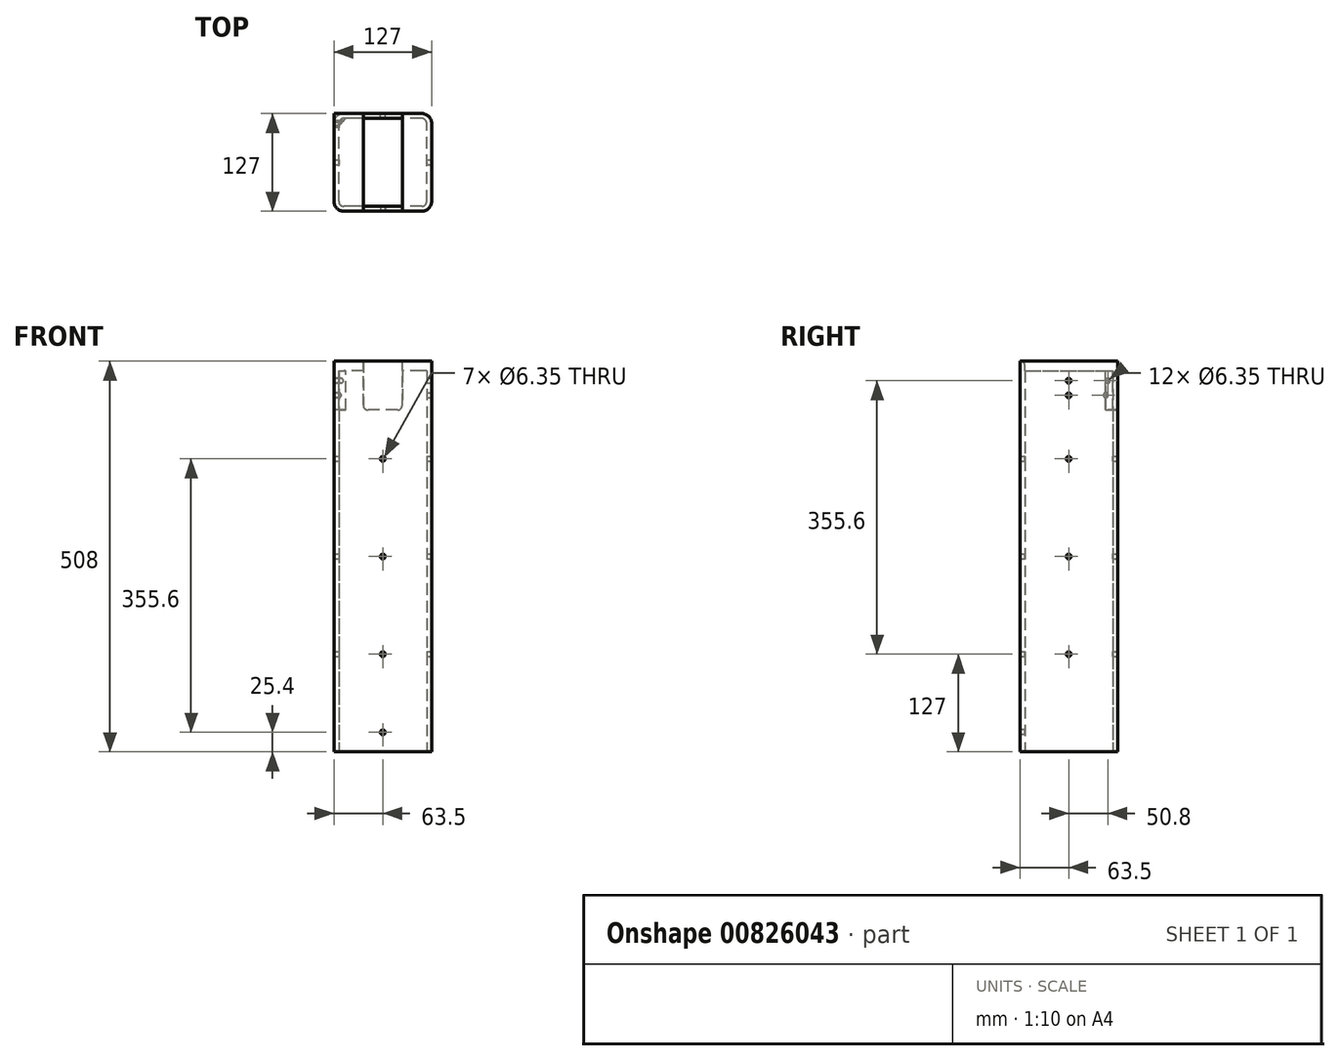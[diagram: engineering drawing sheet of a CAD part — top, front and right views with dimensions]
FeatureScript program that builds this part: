
annotation { "Feature Type Name" : "Feature", "Feature Type Description" : "" }
export const myFeature = defineFeature(function(context is Context, id is Id, definition is map)
    precondition{}
    {
        {
            var Q0;
            Q0=qCreatedBy(makeId("Top.planeOp"),FACE);
            var sketch = newSketch(context, id + "F0", { "sketchPlane" : qUnion([Q0])});
            skLineSegment(sketch, "E0.bottom", {"start": v(50.8, -63.5) * mm, "end": v(-50.8, -63.5) * mm});
            skLineSegment(sketch, "E0.top", {"start": v(50.8, 63.5) * mm, "end": v(-50.8, 63.5) * mm});
            skLineSegment(sketch, "E0.left", {"start": v(63.5, -50.8) * mm, "end": v(63.5, 50.8) * mm});
            skLineSegment(sketch, "E0.right", {"start": v(-63.5, -50.8) * mm, "end": v(-63.5, 50.8) * mm});
            skPoint(sketch, "E0.middle", {"position": v(0, 0) * mm});
            skPoint(sketch, "E1.visualSharp", {"position": v(-63.5, 63.5) * mm});
            skArc(sketch, "E1.filletArc", {"start": v(-50.8, 63.5) * mm, "mid": v(-59.78, 59.78) * mm, "end": v(-63.5, 50.8) * mm});
            skPoint(sketch, "E2.visualSharp", {"position": v(-63.5, -63.5) * mm});
            skArc(sketch, "E2.filletArc", {"start": v(-63.5, -50.8) * mm, "mid": v(-59.78, -59.78) * mm, "end": v(-50.8, -63.5) * mm});
            skPoint(sketch, "E3.visualSharp", {"position": v(63.5, 63.5) * mm});
            skArc(sketch, "E3.filletArc", {"start": v(63.5, 50.8) * mm, "mid": v(59.78, 59.78) * mm, "end": v(50.8, 63.5) * mm});
            skPoint(sketch, "E4.visualSharp", {"position": v(63.5, -63.5) * mm});
            skArc(sketch, "E4.filletArc", {"start": v(50.8, -63.5) * mm, "mid": v(59.78, -59.78) * mm, "end": v(63.5, -50.8) * mm});
            skArc(sketch, "E5.0", {"start": v(57.15, 50.8) * mm, "mid": v(55.3, 55.3) * mm, "end": v(50.8, 57.15) * mm});
            skLineSegment(sketch, "E5.1", {"start": v(57.15, -50.8) * mm, "end": v(57.15, 50.8) * mm});
            skLineSegment(sketch, "E5.2", {"start": v(50.8, 57.15) * mm, "end": v(-50.8, 57.15) * mm});
            skArc(sketch, "E5.3", {"start": v(50.8, -57.15) * mm, "mid": v(55.3, -55.3) * mm, "end": v(57.15, -50.8) * mm});
            skArc(sketch, "E5.4", {"start": v(-50.8, 57.15) * mm, "mid": v(-55.3, 55.3) * mm, "end": v(-57.15, 50.8) * mm});
            skLineSegment(sketch, "E5.5", {"start": v(-57.15, -50.8) * mm, "end": v(-57.15, 50.8) * mm});
            skArc(sketch, "E5.6", {"start": v(-57.15, -50.8) * mm, "mid": v(-55.3, -55.3) * mm, "end": v(-50.8, -57.15) * mm});
            skLineSegment(sketch, "E5.7", {"start": v(50.8, -57.15) * mm, "end": v(-50.8, -57.15) * mm});
            skSolve(sketch);
        }
        {
            var Q0;
            Q0 = qSketchRegion(id + "F0", true);
            extrude(context, id + "F1", {"entities" : qUnion([Q0]), "depth" : 254 * mm, "offsetDistance" : 25.4 * mm, "hasSecondDirection" : true, "secondDirectionOppositeDirection" : true, "secondDirectionDepth" : 254 * mm});
        }
        {
            var Q0;
            Q0=qCreatedBy(makeId("Front.planeOp"),FACE);
            var sketch = newSketch(context, id + "F2", { "sketchPlane" : qUnion([Q0])});
            skLineSegment(sketch, "E6.0", {"start": v(-63.5, 254) * mm, "end": v(63.5, 254) * mm});
            skLineSegment(sketch, "E7.0", {"start": v(-63.5, -0.89) * mm, "end": v(63.5, -0.89) * mm});
            skLineSegment(sketch, "E8", {"start": v(63.5, 236.04) * mm, "end": v(63.5, -0.89) * mm});
            skLineSegment(sketch, "E9", {"start": v(-63.5, 254) * mm, "end": v(-63.5, -0.89) * mm});
            skLineSegment(sketch, "E10", {"start": v(63.5, 254) * mm, "end": v(70.9, 261.4) * mm});
            skLineSegment(sketch, "E11.0", {"start": v(63.5, 236.04) * mm, "end": v(79.88, 252.42) * mm});
            skLineSegment(sketch, "E12", {"start": v(81.46, 262.98) * mm, "end": v(67.93, 249.45) * mm, "construction": true});
            skLineSegment(sketch, "E13", {"start": v(72.48, 262.98) * mm, "end": v(81.46, 262.98) * mm, "construction": true});
            skArc(sketch, "E14", {"start": v(83.16, 254.16) * mm, "mid": v(87.81, 269.33) * mm, "end": v(72.64, 264.68) * mm});
            skPoint(sketch, "E15.visualSharp", {"position": v(72.48, 262.98) * mm});
            skArc(sketch, "E15.filletArc", {"start": v(70.9, 261.4) * mm, "mid": v(72.02, 262.91) * mm, "end": v(72.64, 264.68) * mm});
            skPoint(sketch, "E16.visualSharp", {"position": v(81.46, 254) * mm});
            skArc(sketch, "E16.filletArc", {"start": v(83.16, 254.16) * mm, "mid": v(81.4, 253.54) * mm, "end": v(79.88, 252.42) * mm});
            skLineSegment(sketch, "E17", {"start": v(57.15, 254) * mm, "end": v(57.15, 236.04) * mm});
            skLineSegment(sketch, "E18", {"start": v(57.15, 236.04) * mm, "end": v(63.5, 236.04) * mm});
            skArc(sketch, "E19.0", {"start": v(76.08, 248.62) * mm, "mid": v(92.3, 273.82) * mm, "end": v(67.1, 257.6) * mm});
            skSolve(sketch);
        }
        {
            var Q0;
            Q0=makeQuery(id+"F1.opExtrude","CAP_FACE",FACE,{"disambiguationData":[OSD([sQuery(id+"F0.wireOp",EDGE,"E0.bottom"),sQuery(id+"F0.wireOp",EDGE,"E0.top"),sQuery(id+"F0.wireOp",EDGE,"E0.left"),sQuery(id+"F0.wireOp",EDGE,"E0.right"),sQuery(id+"F0.wireOp",EDGE,"E1.filletArc"),sQuery(id+"F0.wireOp",EDGE,"E2.filletArc"),sQuery(id+"F0.wireOp",EDGE,"E3.filletArc"),sQuery(id+"F0.wireOp",EDGE,"E4.filletArc"),sQuery(id+"F0.wireOp",EDGE,"E5.0"),sQuery(id+"F0.wireOp",EDGE,"E5.1"),sQuery(id+"F0.wireOp",EDGE,"E5.2"),sQuery(id+"F0.wireOp",EDGE,"E5.3"),sQuery(id+"F0.wireOp",EDGE,"E5.4"),sQuery(id+"F0.wireOp",EDGE,"E5.5"),sQuery(id+"F0.wireOp",EDGE,"E5.6"),sQuery(id+"F0.wireOp",EDGE,"E5.7")])],"isStart":false});
            var sketch = newSketch(context, id + "F3", { "sketchPlane" : qUnion([Q0])});
            skLineSegment(sketch, "E20", {"start": v(-63.5, 6.35) * mm, "end": v(-63.5, 50.8) * mm});
            skLineSegment(sketch, "E21", {"start": v(-63.5, -6.35) * mm, "end": v(-63.5, 6.35) * mm});
            skLineSegment(sketch, "E22", {"start": v(-63.5, -50.8) * mm, "end": v(-63.5, -6.35) * mm});
            skArc(sketch, "E23", {"start": v(-63.5, -50.8) * mm, "mid": v(-59.78, -59.78) * mm, "end": v(-50.8, -63.5) * mm});
            skLineSegment(sketch, "E24", {"start": v(50.8, -63.5) * mm, "end": v(25.4, -63.5) * mm});
            skArc(sketch, "E25", {"start": v(50.8, -63.5) * mm, "mid": v(59.78, -59.78) * mm, "end": v(63.5, -50.8) * mm});
            skLineSegment(sketch, "E26", {"start": v(63.5, -50.8) * mm, "end": v(63.5, -6.35) * mm});
            skLineSegment(sketch, "E27", {"start": v(63.5, -6.35) * mm, "end": v(63.5, 6.35) * mm});
            skLineSegment(sketch, "E28", {"start": v(63.5, 6.35) * mm, "end": v(63.5, 50.8) * mm});
            skArc(sketch, "E29", {"start": v(63.5, 50.8) * mm, "mid": v(59.78, 59.78) * mm, "end": v(50.8, 63.5) * mm});
            skLineSegment(sketch, "E30", {"start": v(50.8, 63.5) * mm, "end": v(25.4, 63.5) * mm});
            skArc(sketch, "E31", {"start": v(-50.8, 63.5) * mm, "mid": v(-59.78, 59.78) * mm, "end": v(-63.5, 50.8) * mm});
            skLineSegment(sketch, "E32", {"start": v(-25.4, -63.5) * mm, "end": v(-25.4, 63.5) * mm});
            skLineSegment(sketch, "E33", {"start": v(25.4, -63.5) * mm, "end": v(25.4, 63.5) * mm});
            skLineSegment(sketch, "E34.trimOffspring", {"start": v(-25.4, -63.5) * mm, "end": v(-50.8, -63.5) * mm});
            skLineSegment(sketch, "E35.trimOffspring", {"start": v(-25.4, 63.5) * mm, "end": v(-50.8, 63.5) * mm});
            skSolve(sketch);
        }
        {
            var Q0;
            {var subQ1=makeQuery(id+"F1.opExtrude","CAP_EDGE",EDGE,{"disambiguationData":[OSD([sQuery(id+"F0.wireOp",EDGE,"E5.0")])],"isStart":false});Q0=makeQuery(id+"F3.imprint","IMPRINT",FACE,{"disambiguationData":[TD([[makeQuery(id+"F3.imprint","IMPRINT",EDGE,{"derivedFrom":subQ1}),1.0]])]});}
            var Q1;
            {var subQ1=makeQuery(id+"F1.opExtrude","CAP_EDGE",EDGE,{"disambiguationData":[OSD([sQuery(id+"F0.wireOp",EDGE,"E5.4")])],"isStart":false});Q1=makeQuery(id+"F3.imprint","IMPRINT",FACE,{"disambiguationData":[TD([[makeQuery(id+"F3.imprint","IMPRINT",EDGE,{"derivedFrom":subQ1}),1.0]])]});}
            extrude(context, id + "F4", {"entities" : qUnion([Q0, Q1]), "operationType" : NewBodyOperationType.ADD, "oppositeDirection" : true, "depth" : 12.7 * mm, "offsetDistance" : 25.4 * mm});
        }
        {
            var Q0;
            Q0=makeQuery(id+"F1.opExtrude","SWEPT_FACE",FACE,{"disambiguationData":[OSD([sQuery(id+"F0.wireOp",EDGE,"E0.left")])]});
            var sketch = newSketch(context, id + "F5", { "sketchPlane" : qUnion([Q0])});
            skPoint(sketch, "E36", {"position": v(0, 228.6) * mm});
            skPoint(sketch, "E37", {"position": v(0, 209.55) * mm});
            skSolve(sketch);
        }
        {
            var Q0;
            Q0=sQuery(id+"F5.wireOp",VERTEX,"E37");
            var Q1;
            Q1=sQuery(id+"F5.wireOp",VERTEX,"E36");
            var Q2;
            Q2=makeQuery(id+"F1.opExtrude","SWEPT_BODY",BODY,{"disambiguationData":[OSD([sQuery(id+"F0.wireOp",EDGE,"E0.bottom"),sQuery(id+"F0.wireOp",EDGE,"E0.top"),sQuery(id+"F0.wireOp",EDGE,"E0.left"),sQuery(id+"F0.wireOp",EDGE,"E0.right"),sQuery(id+"F0.wireOp",EDGE,"E1.filletArc"),sQuery(id+"F0.wireOp",EDGE,"E2.filletArc"),sQuery(id+"F0.wireOp",EDGE,"E3.filletArc"),sQuery(id+"F0.wireOp",EDGE,"E4.filletArc"),sQuery(id+"F0.wireOp",EDGE,"E5.0"),sQuery(id+"F0.wireOp",EDGE,"E5.1"),sQuery(id+"F0.wireOp",EDGE,"E5.2"),sQuery(id+"F0.wireOp",EDGE,"E5.3"),sQuery(id+"F0.wireOp",EDGE,"E5.4"),sQuery(id+"F0.wireOp",EDGE,"E5.5"),sQuery(id+"F0.wireOp",EDGE,"E5.6"),sQuery(id+"F0.wireOp",EDGE,"E5.7")])]});
            hole(context, id + "F6", {"style" : HoleStyle.SIMPLE, "endStyle" : HoleEndStyle.THROUGH, "holeDiameter" : 6.35 * mm, "majorDiameter" : 6.35 * mm, "isTappedThrough" : true, "tappedDepth" : 12.7 * mm, "tapClearance" : 3, "locations" : qUnion([Q0, Q1]), "scope" : qUnion([Q2])});
        }
        {
            var Q0;
            Q0=makeQuery(id+"F1.opExtrude","SWEPT_FACE",FACE,{"disambiguationData":[OSD([sQuery(id+"F0.wireOp",EDGE,"E0.bottom")])]});
            var sketch = newSketch(context, id + "F7", { "sketchPlane" : qUnion([Q0])});
            skPoint(sketch, "E38", {"position": v(0, -228.6) * mm});
            skSolve(sketch);
        }
        {
            var Q0;
            Q0=sQuery(id+"F7.wireOp",VERTEX,"E38");
            var Q1;
            Q1=makeQuery(id+"F1.opExtrude","SWEPT_BODY",BODY,{"disambiguationData":[OSD([sQuery(id+"F0.wireOp",EDGE,"E0.bottom"),sQuery(id+"F0.wireOp",EDGE,"E0.top"),sQuery(id+"F0.wireOp",EDGE,"E0.left"),sQuery(id+"F0.wireOp",EDGE,"E0.right"),sQuery(id+"F0.wireOp",EDGE,"E1.filletArc"),sQuery(id+"F0.wireOp",EDGE,"E2.filletArc"),sQuery(id+"F0.wireOp",EDGE,"E3.filletArc"),sQuery(id+"F0.wireOp",EDGE,"E4.filletArc"),sQuery(id+"F0.wireOp",EDGE,"E5.0"),sQuery(id+"F0.wireOp",EDGE,"E5.1"),sQuery(id+"F0.wireOp",EDGE,"E5.2"),sQuery(id+"F0.wireOp",EDGE,"E5.3"),sQuery(id+"F0.wireOp",EDGE,"E5.4"),sQuery(id+"F0.wireOp",EDGE,"E5.5"),sQuery(id+"F0.wireOp",EDGE,"E5.6"),sQuery(id+"F0.wireOp",EDGE,"E5.7")])]});
            hole(context, id + "F8", {"style" : HoleStyle.SIMPLE, "endStyle" : HoleEndStyle.BLIND, "holeDiameter" : 6.35 * mm, "majorDiameter" : 6.35 * mm, "holeDepth" : 12.7 * mm, "isTappedThrough" : true, "tappedDepth" : 12.7 * mm, "tapClearance" : 3, "locations" : qUnion([Q0]), "scope" : qUnion([Q1])});
        }
        {
            var Q0;
            Q0=makeQuery(id+"F1.opExtrude","SWEPT_FACE",FACE,{"disambiguationData":[OSD([sQuery(id+"F0.wireOp",EDGE,"E0.left")])]});
            var sketch = newSketch(context, id + "F9", { "sketchPlane" : qUnion([Q0])});
            skPoint(sketch, "E39", {"position": v(0, 0) * mm});
            skPoint(sketch, "E40", {"position": v(0, 127) * mm});
            skPoint(sketch, "E41", {"position": v(0, -127) * mm});
            skSolve(sketch);
        }
        {
            var Q0;
            Q0=sQuery(id+"F9.wireOp",VERTEX,"E39");
            var Q1;
            Q1=sQuery(id+"F9.wireOp",VERTEX,"E41");
            var Q2;
            Q2=sQuery(id+"F9.wireOp",VERTEX,"E40");
            var Q3;
            Q3=makeQuery(id+"F1.opExtrude","SWEPT_BODY",BODY,{"disambiguationData":[OSD([sQuery(id+"F0.wireOp",EDGE,"E0.bottom"),sQuery(id+"F0.wireOp",EDGE,"E0.top"),sQuery(id+"F0.wireOp",EDGE,"E0.left"),sQuery(id+"F0.wireOp",EDGE,"E0.right"),sQuery(id+"F0.wireOp",EDGE,"E1.filletArc"),sQuery(id+"F0.wireOp",EDGE,"E2.filletArc"),sQuery(id+"F0.wireOp",EDGE,"E3.filletArc"),sQuery(id+"F0.wireOp",EDGE,"E4.filletArc"),sQuery(id+"F0.wireOp",EDGE,"E5.0"),sQuery(id+"F0.wireOp",EDGE,"E5.1"),sQuery(id+"F0.wireOp",EDGE,"E5.2"),sQuery(id+"F0.wireOp",EDGE,"E5.3"),sQuery(id+"F0.wireOp",EDGE,"E5.4"),sQuery(id+"F0.wireOp",EDGE,"E5.5"),sQuery(id+"F0.wireOp",EDGE,"E5.6"),sQuery(id+"F0.wireOp",EDGE,"E5.7")])]});
            hole(context, id + "F10", {"style" : HoleStyle.SIMPLE, "endStyle" : HoleEndStyle.THROUGH, "holeDiameter" : 6.35 * mm, "majorDiameter" : 6.35 * mm, "isTappedThrough" : true, "tappedDepth" : 12.7 * mm, "tapClearance" : 3, "locations" : qUnion([Q0, Q1, Q2]), "scope" : qUnion([Q3])});
        }
        {
            var Q0;
            Q0=makeQuery(id+"F1.opExtrude","SWEPT_FACE",FACE,{"disambiguationData":[OSD([sQuery(id+"F0.wireOp",EDGE,"E0.top")])]});
            var sketch = newSketch(context, id + "F11", { "sketchPlane" : qUnion([Q0])});
            skPoint(sketch, "E42", {"position": v(0, 0) * mm});
            skPoint(sketch, "E43", {"position": v(0, 127) * mm});
            skPoint(sketch, "E44", {"position": v(0, -127) * mm});
            skSolve(sketch);
        }
        {
            var Q0;
            Q0=sQuery(id+"F11.wireOp",VERTEX,"E42");
            var Q1;
            Q1=sQuery(id+"F11.wireOp",VERTEX,"E44");
            var Q2;
            Q2=sQuery(id+"F11.wireOp",VERTEX,"E43");
            var Q3;
            Q3=makeQuery(id+"F1.opExtrude","SWEPT_BODY",BODY,{"disambiguationData":[OSD([sQuery(id+"F0.wireOp",EDGE,"E0.bottom"),sQuery(id+"F0.wireOp",EDGE,"E0.top"),sQuery(id+"F0.wireOp",EDGE,"E0.left"),sQuery(id+"F0.wireOp",EDGE,"E0.right"),sQuery(id+"F0.wireOp",EDGE,"E1.filletArc"),sQuery(id+"F0.wireOp",EDGE,"E2.filletArc"),sQuery(id+"F0.wireOp",EDGE,"E3.filletArc"),sQuery(id+"F0.wireOp",EDGE,"E4.filletArc"),sQuery(id+"F0.wireOp",EDGE,"E5.0"),sQuery(id+"F0.wireOp",EDGE,"E5.1"),sQuery(id+"F0.wireOp",EDGE,"E5.2"),sQuery(id+"F0.wireOp",EDGE,"E5.3"),sQuery(id+"F0.wireOp",EDGE,"E5.4"),sQuery(id+"F0.wireOp",EDGE,"E5.5"),sQuery(id+"F0.wireOp",EDGE,"E5.6"),sQuery(id+"F0.wireOp",EDGE,"E5.7")])]});
            hole(context, id + "F12", {"style" : HoleStyle.SIMPLE, "endStyle" : HoleEndStyle.THROUGH, "holeDiameter" : 6.35 * mm, "majorDiameter" : 6.35 * mm, "isTappedThrough" : true, "tappedDepth" : 12.7 * mm, "tapClearance" : 3, "locations" : qUnion([Q0, Q1, Q2]), "scope" : qUnion([Q3])});
        }
        {
            var Q0;
            Q0=makeQuery(id+"F1.opExtrude","SWEPT_FACE",FACE,{"disambiguationData":[OSD([sQuery(id+"F0.wireOp",EDGE,"E0.top")])]});
            var sketch = newSketch(context, id + "F13", { "sketchPlane" : qUnion([Q0])});
            skLineSegment(sketch, "E45", {"start": v(25.4, 254) * mm, "end": v(25.4, 196.85) * mm});
            skLineSegment(sketch, "E46", {"start": v(19.05, 190.5) * mm, "end": v(-19.05, 190.5) * mm});
            skLineSegment(sketch, "E47", {"start": v(-25.4, 196.85) * mm, "end": v(-25.4, 254) * mm});
            skPoint(sketch, "E48.visualSharp", {"position": v(25.4, 190.5) * mm});
            skArc(sketch, "E48.filletArc", {"start": v(19.05, 190.5) * mm, "mid": v(23.54, 192.36) * mm, "end": v(25.4, 196.85) * mm});
            skPoint(sketch, "E49.visualSharp", {"position": v(-25.4, 190.5) * mm});
            skArc(sketch, "E49.filletArc", {"start": v(-25.4, 196.85) * mm, "mid": v(-23.54, 192.36) * mm, "end": v(-19.05, 190.5) * mm});
            skLineSegment(sketch, "E50", {"start": v(25.4, 254) * mm, "end": v(-25.4, 254) * mm});
            skSolve(sketch);
        }
        {
            var Q0;
            Q0=makeQuery(id+"F13.imprint","IMPRINT",FACE,{"disambiguationData":[TD([[makeQuery(id+"F13.imprint","IMPRINT",EDGE,{"derivedFrom":sQuery(id+"F13.wireOp",EDGE,"E45")}),-1.0]])]});
            extrude(context, id + "F14", {"entities" : qUnion([Q0]), "operationType" : NewBodyOperationType.REMOVE, "oppositeDirection" : true, "depth" : 25.4 * mm, "offsetDistance" : 25.4 * mm});
        }
        {
            var Q0;
            Q0=makeQuery(id+"F14.boolean.opBoolean","COPY",EDGE,{"derivedFrom":makeQuery(id+"F14.opExtrude","CAP_EDGE",EDGE,{"disambiguationData":[OSD([sQuery(id+"F13.wireOp",EDGE,"E47")])],"isStart":true})});
            var Q1;
            Q1=makeQuery(id+"F14.boolean.opBoolean","MERGE",EDGE,{"derivedFrom":[makeQuery(id+"F4.opExtrude","CAP_EDGE",EDGE,{"disambiguationData":[OSD([sQuery(id+"F3.wireOp",EDGE,"E32")])],"isStart":true}),makeQuery(id+"F14.opExtrude","SWEPT_EDGE",EDGE,{"disambiguationData":[OSD([sQuery(id+"F0.wireOp",EDGE,"E0.top"),sQuery(id+"F13.wireOp",EDGE,"E45"),sQuery(id+"F13.wireOp",EDGE,"E50")])]})]});
            var Q2;
            Q2=makeQuery(id+"F14.boolean.opBoolean","MERGE",EDGE,{"derivedFrom":[makeQuery(id+"F4.opExtrude","CAP_EDGE",EDGE,{"disambiguationData":[OSD([sQuery(id+"F3.wireOp",EDGE,"E33")])],"isStart":true}),makeQuery(id+"F14.opExtrude","SWEPT_EDGE",EDGE,{"disambiguationData":[OSD([sQuery(id+"F0.wireOp",EDGE,"E0.top"),sQuery(id+"F13.wireOp",EDGE,"E47"),sQuery(id+"F13.wireOp",EDGE,"E50")])]})]});
            var Q3;
            Q3=makeQuery(id+"F1.opExtrude","CAP_EDGE",EDGE,{"disambiguationData":[OSD([sQuery(id+"F0.wireOp",EDGE,"E5.7")])],"isStart":false});
            fillet(context, id + "F15", {"entities" : qUnion([Q0, Q1, Q2, Q3]), "radius" : 5.08 * mm, "tangentPropagation" : true, "allowEdgeOverflow" : false});
        }
        {
            var Q0;
            {var subQ0=sQuery(id+"F0.wireOp",EDGE,"E5.7");var subQ1=sQuery(id+"F0.wireOp",EDGE,"E5.3");var subQ2=sQuery(id+"F0.wireOp",EDGE,"E5.2");var subQ3=sQuery(id+"F0.wireOp",EDGE,"E5.1");var subQ4=sQuery(id+"F0.wireOp",EDGE,"E5.0");var subQ5=sQuery(id+"F0.wireOp",EDGE,"E5.6");var subQ6=sQuery(id+"F0.wireOp",EDGE,"E5.5");var subQ7=sQuery(id+"F0.wireOp",EDGE,"E5.4");Q0=makeQuery(id+"F4.boolean.opBoolean","MERGE",FACE,{"derivedFrom":[makeQuery(id+"F1.opExtrude","CAP_FACE",FACE,{"disambiguationData":[OSD([sQuery(id+"F0.wireOp",EDGE,"E0.bottom"),sQuery(id+"F0.wireOp",EDGE,"E0.top"),sQuery(id+"F0.wireOp",EDGE,"E0.left"),sQuery(id+"F0.wireOp",EDGE,"E0.right"),sQuery(id+"F0.wireOp",EDGE,"E1.filletArc"),sQuery(id+"F0.wireOp",EDGE,"E2.filletArc"),sQuery(id+"F0.wireOp",EDGE,"E3.filletArc"),sQuery(id+"F0.wireOp",EDGE,"E4.filletArc"),subQ4,subQ3,subQ2,subQ1,subQ7,subQ6,subQ5,subQ0])],"isStart":false}),makeQuery(id+"F4.opExtrude","CAP_FACE",FACE,{"disambiguationData":[OSD([subQ2,subQ7,subQ6,subQ5,subQ0,sQuery(id+"F3.wireOp",EDGE,"E32")])],"isStart":true}),makeQuery(id+"F4.opExtrude","CAP_FACE",FACE,{"disambiguationData":[OSD([subQ4,subQ3,subQ2,subQ1,subQ0,sQuery(id+"F3.wireOp",EDGE,"E33")])],"isStart":true})]});}
            var sketch = newSketch(context, id + "F16", { "sketchPlane" : qUnion([Q0])});
            skArc(sketch, "E51.0", {"start": v(63.5, 50.8) * mm, "mid": v(59.78, 59.78) * mm, "end": v(50.8, 63.5) * mm});
            skPoint(sketch, "E51.1", {"position": v(59.78, 59.78) * mm});
            skLineSegment(sketch, "E52", {"start": v(-63.5, 41.82) * mm, "end": v(-41.82, 63.5) * mm});
            skLineSegment(sketch, "E53", {"start": v(-63.5, 63.5) * mm, "end": v(-41.82, 63.5) * mm});
            skLineSegment(sketch, "E54", {"start": v(-63.5, 41.82) * mm, "end": v(-63.5, 63.5) * mm});
            skSolve(sketch);
        }
        {
            var Q0;
            Q0=makeQuery(id+"F16.imprint","IMPRINT",FACE,{"disambiguationData":[TD([[makeQuery(id+"F16.imprint","IMPRINT",EDGE,{"derivedFrom":sQuery(id+"F16.wireOp",EDGE,"XSHbPfwL-9F1J-AFW9-hyfD-QW67k0lzLT0j")}),-1.0]])]});
            var Q1;
            {var subQ0=sQuery(id+"F16.wireOp",EDGE,"E52");Q1=makeQuery(id+"F16.imprint","IMPRINT",FACE,{"disambiguationData":[TD([[makeQuery(id+"F16.imprint","IMPRINT",EDGE,{"derivedFrom":subQ0}),1.0]])]});}
            var Q2;
            {var subQ1=makeQuery(id+"F1.opExtrude","CAP_EDGE",EDGE,{"disambiguationData":[OSD([sQuery(id+"F0.wireOp",EDGE,"E1.filletArc")])],"isStart":false});Q2=makeQuery(id+"F16.imprint","IMPRINT",FACE,{"disambiguationData":[TD([[makeQuery(id+"F16.imprint","IMPRINT",EDGE,{"derivedFrom":subQ1}),-1.0]])]});}
            extrude(context, id + "F17", {"entities" : qUnion([Q0, Q1, Q2]), "operationType" : NewBodyOperationType.ADD, "oppositeDirection" : true, "depth" : 63.5 * mm, "offsetDistance" : 25.4 * mm});
        }
        {
            var Q0;
            Q0=makeQuery(id+"F17.boolean.opBoolean","MERGE",FACE,{"derivedFrom":[makeQuery(id+"F1.opExtrude","SWEPT_FACE",FACE,{"disambiguationData":[OSD([sQuery(id+"F0.wireOp",EDGE,"E0.right")])]}),makeQuery(id+"F17.opExtrude","SWEPT_FACE",FACE,{"disambiguationData":[OSD([sQuery(id+"F16.wireOp",EDGE,"E54")])]})]});
            var sketch = newSketch(context, id + "F18", { "sketchPlane" : qUnion([Q0])});
            skPoint(sketch, "E55", {"position": v(-50.8, 228.6) * mm});
            skPoint(sketch, "E56", {"position": v(-48.26, 209.72) * mm});
            skSolve(sketch);
        }
        {
            var Q0;
            Q0=sQuery(id+"F18.wireOp",VERTEX,"E56");
            var Q1;
            Q1=sQuery(id+"F18.wireOp",VERTEX,"E55");
            var Q2;
            Q2=makeQuery(id+"F1.opExtrude","SWEPT_BODY",BODY,{"disambiguationData":[OSD([sQuery(id+"F0.wireOp",EDGE,"E0.bottom"),sQuery(id+"F0.wireOp",EDGE,"E0.top"),sQuery(id+"F0.wireOp",EDGE,"E0.left"),sQuery(id+"F0.wireOp",EDGE,"E0.right"),sQuery(id+"F0.wireOp",EDGE,"E1.filletArc"),sQuery(id+"F0.wireOp",EDGE,"E2.filletArc"),sQuery(id+"F0.wireOp",EDGE,"E3.filletArc"),sQuery(id+"F0.wireOp",EDGE,"E4.filletArc"),sQuery(id+"F0.wireOp",EDGE,"E5.0"),sQuery(id+"F0.wireOp",EDGE,"E5.1"),sQuery(id+"F0.wireOp",EDGE,"E5.2"),sQuery(id+"F0.wireOp",EDGE,"E5.3"),sQuery(id+"F0.wireOp",EDGE,"E5.4"),sQuery(id+"F0.wireOp",EDGE,"E5.5"),sQuery(id+"F0.wireOp",EDGE,"E5.6"),sQuery(id+"F0.wireOp",EDGE,"E5.7")])]});
            hole(context, id + "F19", {"style" : HoleStyle.SIMPLE, "endStyle" : HoleEndStyle.BLIND, "holeDiameter" : 6.35 * mm, "majorDiameter" : 6.35 * mm, "holeDepth" : 12.7 * mm, "isTappedThrough" : true, "tappedDepth" : 12.7 * mm, "tapClearance" : 3, "locations" : qUnion([Q0, Q1]), "scope" : qUnion([Q2])});
        }
    });
